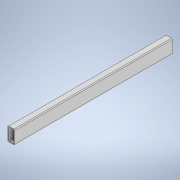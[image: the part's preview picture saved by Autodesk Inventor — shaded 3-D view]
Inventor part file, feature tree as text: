
AUTODESK INVENTOR PART (.ipt)
format: ipt  version: 2020 (Build 240168000, 168)  size: 123,904 bytes
history: native  units: in
note: dims shown in document units (in); Inventor stores cm internally (conversion verified against a paired STEP export)
features: extrude x1, sketch x1
ambient origin geometry x8: Origin, YZ Plane, XZ Plane, XY Plane, X Axis, Y Axis, Z Axis, Center Point
bodies: Solid1 (feature_tree)
feature tree (2):
  extrude  "Extrusion1"  Depth=1.0in
  sketch  "Sketch1"  dims[d0=2.0in d1=1.0in d2=0.125in d3=0.125in d4=0.125in d5=0.125in d6=0.125in d7=0.125in d8=0.125in d9=0.125in d10=0.125in d11=23.0in d12=0.0in]
